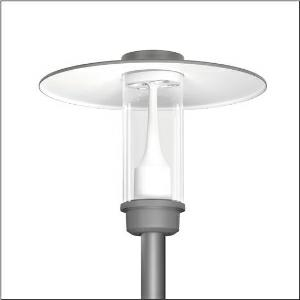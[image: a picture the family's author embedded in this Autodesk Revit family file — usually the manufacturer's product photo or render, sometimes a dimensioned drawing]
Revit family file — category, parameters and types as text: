
# Revit family: litepole_2_iq___st1_2a_5xa5425ef14hp_0eb2
name_source: partatom
category: Lighting Fixtures
units: mm (PartAtom-declared; Revit-internal decimal feet)

## family parameters
Cut with Voids When Loaded = No
Host = Face
Light Source = No
Part Type = Normal
Room Calculation Point = No
Round Connector Dimension = Use Diameter
Shared = No

## types (1)
- --- (1 x LED, 4760 lm, 33.6 W, 3000K)
    Apparent Load = 34 VA
    CIE Flux Codes = 22 59 92 98 100
    Color Rendering = 70
    Color Temperature = 3000K
    Default Elevation = 1800 mm
    Description = Litepole 2 iQ, mast luminaire, Module 540 iQ-SR, primary light control with 3 zone facetted reflector, of plastic, silver coated, highly specular, structured, primary optical cover: cover, of PMMA, transparent, light distribution: ST1.2a, light emission: direct distribution, primary light characteristic: asymmetric, installation type: post-top, LED, High Power LED, rated luminous flux: 4.760lm, luminous efficacy: 142lm/W, light colour: 730, colour temperature: 3000K, control gear: iQ Street-Remote, control: pre-setting: logarithmic dimming characteristic, Street-Remote, Auto-Match, Temp-Guard, Lumen-Switch, Night-Set, Smart-Wire, Light-Fading, Desk-Remote (wireless, voltage-free reading and setting of iQ features in the workshop via application-optimized NFC function/RFID function), optimised constant luminous flux control (CLO 2.0), with terminal, 6-pole, max. 2.5mm², mains connection: 230..240V, AC, 50/60Hz, start of lifetime: 34W, end of service life: 36W, reduction: 15W, luminaire housing, upper part, of aluminium, coated, Siteco® metallic grey (DB 702S), diameter: 750mm, height: 590mm, spigot size: d x l = 76 x 70mm (post-top) | with reducer (optional accessory) 60 x 70mm, mounting height: 3..5m, post-top mast mounting element, of diecast aluminium, coated, Siteco® metallic grey (DB 702S), Module 540 iQ-SR, traffic white (RAL 9016), equipment: Power, protection rating (complete): IP65, insulation class (complete): insulation class II (safety insulation), certification: CE, ENEC, VDE, packaging unit: 1 piece

Light Distribution: ST1.2a
    Height = 590 mm
    Lamp = 1 x LED
    Lamp Light Flux = 4760 lm
    Lamp Power = 33.6 W
    Lamp count = 1
    Length = 750 mm
    Luminous efficacy = 142 lm/W
    Manufacturer = Siteco
    ModVariant = No
    Model = 5XA5425EF14HP
    Number of Poles = 1
    OnlyDefault = Yes
    Power Factor = 1
    Product Name = Litepole 2 iQ | ST1.2a
    Product group = mast luminaire | pylon top
    ProductGroupID = 6100
    Protection Class = Protection class II
    Protection Degree = IP 65
    RLX_Detail_Level = 1
    RLX_Emergency_Light_Flux = 0 lm
    RLX_Emergency_Type = 0
    RLX_Emergency_Type_DB = No
    RlxData = <blob elided: 31949 chars, md5=58f48888>
    Socket = socket
    Standby Power = 0 W
    System Light Flux = 4760 lm
    System Power = 34 W
    Type Comments = factory setting: luminous flux: 100 % | dim-lin: 254 | 695 mA
    Type Image = l_1006518.jpg
    URL = http://relux.com
    VarID = @adj_189723
    Voltage = 0 V
    Weight = 0.00 kg
    Width = 0 mm  [stored 0 ft]

note: [stored X ft] marks values corroborated as IEEE doubles in the binary element streams (Revit-internal decimal feet)

## geometry (parser evidence)
native form markers: Blend x4, Sweep x10
no freeform markers — native parametric forms only
